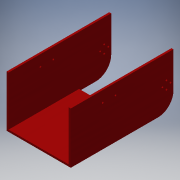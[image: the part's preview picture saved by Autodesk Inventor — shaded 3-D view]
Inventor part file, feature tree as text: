
AUTODESK INVENTOR PART (.ipt)
format: ipt  version: 2016 (Build 200138000, 138)  size: 133,632 bytes
history: native  units: in
note: dims shown in document units (in); Inventor stores cm internally (conversion verified against a paired STEP export)
features: reference x6, sketch x5, extrude x3, hole x2, fillet x1
ambient origin geometry x8: Origin, YZ Plane, XZ Plane, XY Plane, X Axis, Y Axis, Z Axis, Center Point
bodies: Solid1 (feature_tree)
feature tree (17):
  extrude  "Extrusion1"  Depth=8.0in
  extrude  "Extrusion2"  Depth=4.7in
  extrude  "Extrusion3"  Depth=2.5in
  fillet  "Fillet1"  Radius=0.15in
  hole  "Hole2"  [1 undecoded]
  hole  "Hole3"  [1 undecoded]
  sketch  "Sketch1"  dims[d0=5.0in d1=8.0in]
  sketch  "Sketch3"  dims[d2=4.0in d3=0.0in d4=4.7in]
  sketch  "Sketch4"  dims[d5=3.85in d6=0.0in d7=2.5in d8=0.15in d9=0.0in]
  sketch  "Sketch7"  dims[d10=1.2in]
  reference  "Reference12"
  reference  "Reference13"
  reference  "Reference14"
  reference  "Reference15"
  sketch  "Sketch8"  dims[d18=0.1457in d19=0.75in d20=0.375in d21=0.25in d22=0.5635in d23=0.15in d24=0.8108in d25=0.1457in d26=0.75in d27=0.375in d28=0.25in d29=0.5635in d30=0.15in d31=0.8108in]
  reference  "Reference16"
  reference  "Reference17"
note: 2 required parameter values undecoded (feature->parameter linkage not recoverable at this tier; creation-order binding heuristic only, values carry confidence <= 0.55)
